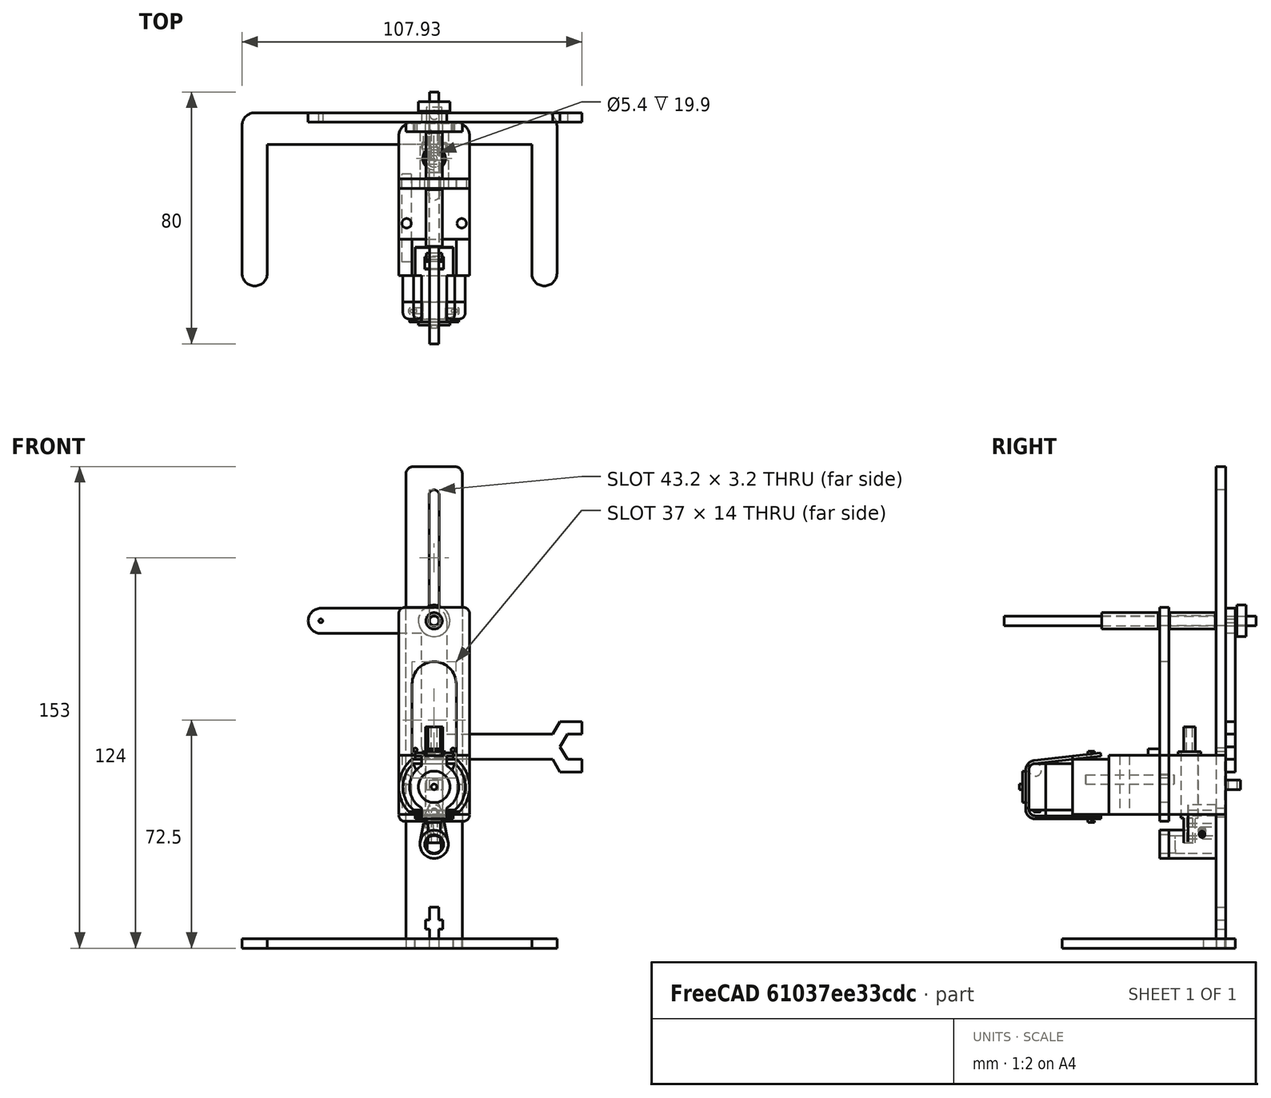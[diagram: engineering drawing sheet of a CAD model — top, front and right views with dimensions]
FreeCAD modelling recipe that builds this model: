
FCSTD DOCUMENT  (FreeCAD 0.21R33771 (Git))
Label: legged_robot_03
License: Other
LicenseURL: https://ohwr.org/project/cernohl/wikis/Documents/CERN-OHL-version-2
objects: PartDesign::Body×23, Part::Feature×19, Sketcher::SketchObject×18, PartDesign::SubShapeBinder×16, PartDesign::Pad×15, PartDesign::CoordinateSystem×12, PartDesign::FeatureBase×9, Part::Part2DObjectPython×7, PartDesign::Plane×6, App::DocumentObjectGroup×4, Part::Compound2×2, PartDesign::Pocket×2, App::FeaturePython×1, App::Part×1, App::LinkGroup×1
note: 144 computed .brp shape members not serialized (recipe doc carries the construction recipe); baked Part::Feature solids carry a one-line shape summary decoded from their .brp

FEATURE [PartDesign::CoordinateSystem] LCS_Origin
  AttacherType = Attacher::AttachEngine3D
  MapMode = 2
  Support = -> [X_Axis025]
FEATURE [App::FeaturePython] Variables  # WARN: FeaturePython — macro-defined, semantics opaque (R4)
  Type = App::PropertyContainer
FEATURE [App::DocumentObjectGroup] Constraints
FEATURE [App::DocumentObjectGroup] Configurations
FEATURE [App::Part] Assembly
  AssemblyType = Part::Link
  Group = -> [LCS_Origin,Variables,Constraints,Configurations]
  Origin = -> Origin025
  Type = Assembly
FEATURE [PartDesign::SubShapeBinder] Binder002
  BindCopyOnChange = 0
  BindMode = 0
  ClaimChildren = false
  Context = -> Parts [Body001.Binder002.]
  Fuse = false
  MakeFace = true
  OffsetFill = false
  OffsetIntersection = false
  OffsetJoinType = 0
  OffsetOpenResult = false
  PartialLoad = false
  Refine = true
  Relative = true
  Support = -> [LinkGroup]
  _Version = 2
FEATURE [PartDesign::CoordinateSystem] motor_mount_urb
  AttacherType = Attacher::AttachEngine3D
  AttachmentOffset = pos=(0,0,0) rot=(0.57735,-0.57735,-0.57735;2.0944rad)
  MapMode = 11
  Placement = pos=(-8.75,-9.5,-7.7) rot=(0,0,1;0rad)
  Support = -> [Binder002]
FEATURE [PartDesign::CoordinateSystem] motor_top_centre
  AttacherType = Attacher::AttachEngine3D
  AttachmentOffset = pos=(0,0,0) rot=(0,0,-1;1.5708rad)
  MapMode = 11
  Placement = pos=(-1.2e-15,-19.55,25.7) rot=(0,0,1;0rad)
  Support = -> [Binder002]
FEATURE [Part::Feature] Shell002
  shape: bbox 8 x 1.776 x 1.987 mm, 1 faces, 0 solids (baked)
FEATURE [Part::Feature] Solid008  label="Part 3"
  shape: bbox 19.8 x 8.5 x 14.8 mm, 6 faces (baked)
FEATURE [Part::Feature] Solid009  label="Part 2"
  shape: bbox 5.4 x 5.4 x 36.8 mm, 15 faces (baked)
FEATURE [PartDesign::CoordinateSystem] motor_mount_urf
  AttacherType = Attacher::AttachEngine3D
  AttachmentOffset = pos=(0,0,0) rot=(-0.57735,-0.57735,0.57735;2.0944rad)
  MapMode = 11
  Placement = pos=(8.75,-9.5,-7.7) rot=(0,0,1;0rad)
  Support = -> [Binder002]
FEATURE [Part::Feature] Solid003  label="Part 8"
  shape: bbox 15.62 x 23.85 x 20.96 mm, 35 faces (baked)
FEATURE [Part::Feature] Solid010  label="Part 1"
  shape: bbox 22.5 x 53.35 x 23.3 mm, 41 faces (baked)
FEATURE [PartDesign::CoordinateSystem] motor_mount_ul  label="motor_mount_ulb"
  AttacherType = Attacher::AttachEngine3D
  AttachmentOffset = pos=(0,0,0) rot=(0.57735,-0.57735,-0.57735;2.0944rad)
  MapMode = 11
  Placement = pos=(-8.75,-28.3,-7.7) rot=(0,0,1;0rad)
  Support = -> [Binder002]
FEATURE [PartDesign::CoordinateSystem] motor_cam_left
  AttacherType = Attacher::AttachEngine3D
  AttachmentOffset = pos=(0,0,0) rot=(0.57735,-0.57735,-0.57735;2.0944rad)
  MapMode = 11
  Placement = pos=(-1e-16,-37.3,-28.3) rot=(0,0,1;0rad)
  Support = -> [Binder002]
FEATURE [PartDesign::CoordinateSystem] motor_cam_right
  AttacherType = Attacher::AttachEngine3D
  AttachmentOffset = pos=(0,0,0) rot=(0.57735,-0.57735,-0.57735;2.0944rad)
  MapMode = 11
  Placement = pos=(-1e-16,-0.499998,-28.3) rot=(0,0,1;0rad)
  Support = -> [Binder002]
FEATURE [Part::Feature] Shell001
  shape: bbox 8 x 21.07 x 2.378 mm, 1 faces, 0 solids (baked)
FEATURE [PartDesign::CoordinateSystem] motor_base_centre
  AttacherType = Attacher::AttachEngine3D
  AttachmentOffset = pos=(0,0,0) rot=(-0.707107,0,-0.707107;3.14159rad)
  MapMode = 45
  Placement = pos=(-6.6e-15,-18.9,-42.1) rot=(0,1.00652,0;0rad)
  Support = -> [Binder002]
FEATURE [Part::Feature] Solid006  label="Part 5"
  shape: bbox 1.8 x 1 x 1.8 mm, 3 faces (baked)
FEATURE [Part::Feature] Solid007  label="Part 4"
  shape: bbox 21.43 x 7.35 x 17.97 mm, 16 faces (baked)
FEATURE [Part::Feature] Shell004
  shape: bbox 8 x 2 x 2 mm, 1 faces, 0 solids (baked)
FEATURE [Part::Feature] Solid004  label="Part 7"
  shape: bbox 4.343 x 2 x 0.1 mm, 16 faces (baked)
FEATURE [Part::Feature] Shell
  shape: bbox 8 x 20.85 x 2e-07 mm, 1 faces, 0 solids (baked)
FEATURE [PartDesign::CoordinateSystem] motor_mount_ulf
  AttacherType = Attacher::AttachEngine3D
  AttachmentOffset = pos=(0,0,0) rot=(-0.57735,-0.57735,0.57735;2.0944rad)
  MapMode = 11
  Placement = pos=(8.75,-28.3,-7.7) rot=(0,0,1;0rad)
  Support = -> [Binder002]
FEATURE [PartDesign::CoordinateSystem] LCS_13
  AttacherType = Attacher::AttachEngine3D
  AttachmentOffset = pos=(0,0,0) rot=(-0.57735,-0.57735,-0.57735;2.0944rad)
  MapMode = 14
  Placement = pos=(11.25,-28.3,-2.65) rot=(0,0,1;0rad)
  Support = -> [Binder002]
FEATURE [PartDesign::Body] Body001  label="Motor001"
  Group = -> [Binder002,motor_cam_left,motor_cam_right,motor_mount_ul,motor_mount_ulf,motor_mount_urb,motor_mount_urf,motor_top_centre,motor_base_centre,LCS_13]
  Origin = -> Origin001
FEATURE [Part::Feature] Solid005  label="Part 6"
  shape: bbox 4.343 x 2 x 0.1 mm, 16 faces (baked)
FEATURE [Part::Feature] Shell003
  shape: bbox 8 x 2e-07 x 12.6 mm, 1 faces, 0 solids (baked)
FEATURE [Part::Compound2] Compound001  label="Surface 1"
  Links = -> [Shell,Shell001,Shell002,Shell003,Shell004]
FEATURE [App::LinkGroup] LinkGroup
  ElementList = -> [Solid003,Compound001,Solid004,Solid005,Solid006,Solid007,Solid008,Solid009,Solid010]
  LinkMode = 0
  Placement = pos=(0,-9.5,-28.3) rot=(-1,0,0;1.5708rad)
FEATURE [Part::Feature] Shell005
  shape: bbox 25.33 x 0.8457 x 15.74 mm, 1 faces, 0 solids (baked)
FEATURE [Part::Feature] Shell006
  shape: bbox 24.78 x 2e-07 x 15.38 mm, 1 faces, 0 solids (baked)
FEATURE [Part::Feature] Shell007
  shape: bbox 26 x 42.82 x 16.6 mm, 188 faces, 0 solids (baked)
FEATURE [Part::Feature] Shell008
  shape: bbox 8.776 x 3 x 7.6 mm, 28 faces, 0 solids (baked)
FEATURE [Part::Feature] Shell009
  shape: bbox 6.35 x 1.5 x 6.35 mm, 2 faces, 0 solids (baked)
FEATURE [Part::Feature] Shell010
  shape: bbox 8 x 3.2 x 8 mm, 10 faces, 0 solids (baked)
FEATURE [Part::Compound2] Compound  label="battery_9V"
  Links = -> [Shell005,Shell006,Shell007,Shell008,Shell009,Shell010]
  Placement = pos=(-25,-19,-18) rot=(0,0.707107,0.707107;3.14159rad)
FEATURE [PartDesign::SubShapeBinder] Binder007
  BindCopyOnChange = 0
  BindMode = 0
  ClaimChildren = false
  Context = -> Parts [Body021.Binder007.]
  Fuse = false
  MakeFace = true
  OffsetFill = false
  OffsetIntersection = false
  OffsetJoinType = 0
  OffsetOpenResult = false
  PartialLoad = false
  Refine = true
  Relative = true
  Support = -> [LinkGroup]
  _Version = 2
FEATURE [Sketcher::SketchObject] Sketch027
  AttachmentOffset = pos=(0,0,2) rot=(0,0,1;0rad)
  ExternalGeometry = -> [Binder007]
  FullyConstrained = true
  MapMode = 5
  Placement = pos=(0,0,20.4) rot=(0,0,1;0rad)
  Support = -> [Binder007]
  sketch-geometry (23):
    g0: Circle CenterX=1.90735e-07 CenterY=27 CenterZ=0 NormalX=0 NormalY=0 NormalZ=1 AngleXU=0 Radius=4.5
    g1: Circle CenterX=10 CenterY=27 CenterZ=0 NormalX=0 NormalY=0 NormalZ=1 AngleXU=0 Radius=0.95
    g2: LineSegment StartX=0.900016 StartY=31.4091 StartZ=0 EndX=10.5 EndY=29.4495 EndZ=0
    g3: ArcOfCircle CenterX=10 CenterY=27 CenterZ=0 NormalX=0 NormalY=0 NormalZ=1 AngleXU=0 Radius=2.5 StartAngle=4.8601 EndAngle=7.65262
    g4: LineSegment StartX=10.3679 StartY=24.5272 StartZ=0 EndX=8.88426 EndY=24.3065 EndZ=0
    g5: ArcOfCircle CenterX=8.58992 CenterY=26.2847 CenterZ=0 NormalX=0 NormalY=0 NormalZ=1 AngleXU=0 Radius=2 StartAngle=3.2893 EndAngle=4.8601
    g6: LineSegment StartX=6.6117 StartY=25.9903 StartZ=0 EndX=6.58226 EndY=26.1882 EndZ=0
    g7: ArcOfCircle CenterX=5.84043 CenterY=26.0778 CenterZ=0 NormalX=0 NormalY=0 NormalZ=1 AngleXU=0 Radius=0.75 StartAngle=0.147708 EndAngle=1.54397
    g8: LineSegment StartX=5.86055 StartY=26.8275 StartZ=0 EndX=2.79854 EndY=26.9097 EndZ=0
    g9: LineSegment StartX=0.781434 StartY=22.5684 StartZ=0 EndX=6.69028 EndY=23.6103 EndZ=0
    g10: LineSegment StartX=6.69028 StartY=23.6103 StartZ=0 EndX=6.534 EndY=24.4966 EndZ=0
    g11: ArcOfCircle CenterX=5.54919 CenterY=24.3229 CenterZ=0 NormalX=0 NormalY=0 NormalZ=1 AngleXU=0 Radius=1 StartAngle=0.174533 EndAngle=1.5708
    g12: LineSegment StartX=5.54919 StartY=25.3229 StartZ=0 EndX=2.67887 EndY=25.3229 EndZ=0
    g13: Circle CenterX=1.90735e-07 CenterY=27 CenterZ=0 NormalX=0 NormalY=0 NormalZ=1 AngleXU=0 Radius=2.8
    g14: LineSegment StartX=1.8 StartY=29.2 StartZ=0 EndX=-1.8 EndY=29.2 EndZ=0
    g15: ArcOfCircle CenterX=-1.8 CenterY=28.2 CenterZ=0 NormalX=0 NormalY=0 NormalZ=1 AngleXU=0 Radius=1 StartAngle=1.5708 EndAngle=3.14159
    g16: LineSegment StartX=-2.8 StartY=28.2 StartZ=0 EndX=-2.8 EndY=25.8 EndZ=0
    g17: ArcOfCircle CenterX=-1.8 CenterY=25.8 CenterZ=0 NormalX=0 NormalY=0 NormalZ=1 AngleXU=0 Radius=1 StartAngle=3.14159 EndAngle=4.71239
    g18: LineSegment StartX=-1.8 StartY=24.8 StartZ=0 EndX=1.8 EndY=24.8 EndZ=0
    g19: ArcOfCircle CenterX=1.8 CenterY=25.8 CenterZ=0 NormalX=0 NormalY=0 NormalZ=1 AngleXU=0 Radius=1 StartAngle=4.71239 EndAngle=6.28319
    g20: LineSegment StartX=2.8 StartY=25.8 StartZ=0 EndX=2.8 EndY=28.2 EndZ=0
    g21: ArcOfCircle CenterX=1.8 CenterY=28.2 CenterZ=0 NormalX=0 NormalY=0 NormalZ=1 AngleXU=0 Radius=1 StartAngle=-1.8e-15 EndAngle=1.5708
    g22: LineSegment StartX=1.90735e-07 StartY=27 StartZ=0 EndX=-2.8 EndY=27 EndZ=0
  constraints (58):
    c: Diameter(g0) = 9
    c: Diameter(g1) = 1.9
    c: Tangent(g2,g3) = 1.5708
    c: Tangent(g4,g5) = 1.5708
    c: Tangent(g6,g7) = -1.5708
    c: Coincident(g9,g10)
    c: Tangent(g10,g11) = -1.5708
    c: Diameter(g3) = 5
    c: Tangent(g2,g0)
    c: PointOnObject(g2,g0)
    c: Tangent(g3,g4) = 1.5708
    c: Angle(g3) = 2.79253
    c: Distance(g4) = 1.5
    c: Diameter(g5) = 4
    c: Angle(g5) = 1.5708
    c: Tangent(g7,g8) = -1.5708
    c: Tangent(g5,g6) = 1.5708
    c: Distance(g6) = 0.2
    c: Diameter(g7) = 1.5
    c: Angle(g7) = 1.39626
    c: PointOnObject(g9,g0)
    c: Diameter(g11) = 2
    c: Distance(g10) = 0.9
    c: Perpendicular(g9,g10)
    c: Tangent(g11,g12) = -1.5708
    c: Angle(g9) = 0.174533
    c: Angle(g11) = 1.39626
    c: Tangent(g9,g0)
    c: Distance(g9) = 6
    c: Coincident(g0,g-3)
    c: Horizontal(g3,g0)
    c: DistanceX(g0,g3) = 10
    c: Coincident(g1,g3)
    c: Coincident(g13,g0)
    c: Diameter(g13) = 5.6
    c: Horizontal(g14)
    c: Tangent(g14,g15) = -1.5708
    c: Vertical(g16)
    c: Tangent(g16,g17) = -1.5708
    c: Horizontal(g18)
    c: Tangent(g18,g19) = -1.5708
    c: Vertical(g20)
    c: Tangent(g20,g21) = -1.5708
    c: Tangent(g21,g14) = -1.5708
    c: Tangent(g19,g20) = -1.5708
    c: Tangent(g17,g18) = -1.5708
    c: Tangent(g15,g16) = -1.5708
    c: Diameter(g19) = 2
    c: Equal(g19,g21)
    c: Equal(g19,g17)
    c: DistanceX(g15,g20) = 5.6
    c: DistanceY(g17,g14) = 4.4
    c: Symmetric(g15,g20,g-2)
    c: Coincident(g22,g0)
    c: PointOnObject(g22,g16)
    c: Symmetric(g14,g17,g22)
    c: PointOnObject(g8,g13)
    c: PointOnObject(g12,g19)
FEATURE [Sketcher::SketchObject] Sketch
  AttachmentOffset = pos=(0,0,2) rot=(0,0,1;0rad)
  ExternalGeometry = -> [Binder007,Sketch027]
  FullyConstrained = true
  MapMode = 5
  Placement = pos=(0,0,12.5) rot=(0,0,1;0rad)
  Support = -> [Binder007]
  sketch-geometry (2):
    g0: Circle CenterX=1.90735e-07 CenterY=27 CenterZ=0 NormalX=0 NormalY=0 NormalZ=1 AngleXU=0 Radius=2.8
    g1: Circle CenterX=1.90735e-07 CenterY=27 CenterZ=0 NormalX=0 NormalY=0 NormalZ=1 AngleXU=0 Radius=4.5
  constraints (4):
    c: Coincident(g0,g-3)
    c: Coincident(g1,g0)
    c: Equal(g0,g-5)
    c: Equal(g-4,g1)
FEATURE [PartDesign::Pad] Pad
  Direction = (1,1,1)
  Length = 2
  Length2 = 100
  Profile = -> Sketch
  Type = 0
FEATURE [Sketcher::SketchObject] Sketch029
  ExternalGeometry = -> [Binder007,Sketch027]
  FullyConstrained = true
  MapMode = 5
  Placement = pos=(3e-15,0,14.5) rot=(0,0,1;0rad)
  Support = -> [Pad]
  sketch-geometry (9):
    g0: Circle CenterX=1.90735e-07 CenterY=27 CenterZ=0 NormalX=0 NormalY=0 NormalZ=1 AngleXU=0 Radius=4.5
    g1: LineSegment StartX=1.8 StartY=29.2 StartZ=0 EndX=-1.8 EndY=29.2 EndZ=0
    g2: ArcOfCircle CenterX=-1.8 CenterY=28.2 CenterZ=0 NormalX=0 NormalY=0 NormalZ=1 AngleXU=0 Radius=1 StartAngle=1.5708 EndAngle=3.14159
    g3: LineSegment StartX=-2.8 StartY=28.2 StartZ=0 EndX=-2.8 EndY=25.8 EndZ=0
    g4: ArcOfCircle CenterX=-1.8 CenterY=25.8 CenterZ=0 NormalX=0 NormalY=0 NormalZ=1 AngleXU=0 Radius=1 StartAngle=3.14159 EndAngle=4.71239
    g5: LineSegment StartX=-1.8 StartY=24.8 StartZ=0 EndX=1.8 EndY=24.8 EndZ=0
    g6: ArcOfCircle CenterX=1.8 CenterY=25.8 CenterZ=0 NormalX=0 NormalY=0 NormalZ=1 AngleXU=0 Radius=1 StartAngle=4.71239 EndAngle=6.28319
    g7: LineSegment StartX=2.8 StartY=25.8 StartZ=0 EndX=2.8 EndY=28.2 EndZ=0
    g8: ArcOfCircle CenterX=1.8 CenterY=28.2 CenterZ=0 NormalX=0 NormalY=0 NormalZ=1 AngleXU=0 Radius=1 StartAngle=-1.8e-15 EndAngle=1.5708
  constraints (17):
    c: Coincident(g0,g-4)
    c: Coincident(g-5,g1)
    c: Coincident(g1,g-5)
    c: Tangent(g1,g2) = -1.5708
    c: Coincident(g3,g-7)
    c: Tangent(g3,g4) = -1.5708
    c: Coincident(g5,g-6)
    c: Tangent(g5,g6) = -1.5708
    c: Coincident(g7,g-8)
    c: Tangent(g7,g8) = -1.5708
    c: Tangent(g2,g3) = -1.5708
    c: Tangent(g4,g5) = -1.5708
    c: Tangent(g6,g7) = -1.5708
    c: Tangent(g8,g1) = -1.5708
    c: Vertical(g3)
    c: Horizontal(g5)
    c: Equal(g0,g-4)
FEATURE [PartDesign::Pad] Pad029
  BaseFeature = -> Pad
  Direction = (1,1,1)
  Length = 4
  Length2 = 100
  Profile = -> Sketch029
  Type = 0
FEATURE [Sketcher::SketchObject] Sketch028
  ExternalGeometry = -> [Sketch027]
  FullyConstrained = true
  MapMode = 5
  Placement = pos=(3.5e-15,0,18.5) rot=(0,0,1;0rad)
  Support = -> [Pad029]
  sketch-geometry (21):
    g0: LineSegment StartX=10.5 StartY=29.4495 StartZ=0 EndX=0.900016 EndY=31.4091 EndZ=0
    g1: ArcOfCircle CenterX=1.69849e-05 CenterY=27 CenterZ=0 NormalX=0 NormalY=0 NormalZ=1 AngleXU=0 Radius=4.5 StartAngle=1.36944 EndAngle=4.88692
    g2: LineSegment StartX=0.781434 StartY=22.5684 StartZ=0 EndX=6.69028 EndY=23.6103 EndZ=0
    g3: LineSegment StartX=6.69028 StartY=23.6103 StartZ=0 EndX=6.534 EndY=24.4966 EndZ=0
    g4: ArcOfCircle CenterX=5.54919 CenterY=24.3229 CenterZ=0 NormalX=0 NormalY=0 NormalZ=1 AngleXU=0 Radius=1 StartAngle=0.174533 EndAngle=1.5708
    g5: LineSegment StartX=5.54919 StartY=25.3229 StartZ=0 EndX=2.8 EndY=25.8 EndZ=0
    g6: ArcOfCircle CenterX=1.59004 CenterY=26.01 CenterZ=0 NormalX=0 NormalY=0 NormalZ=1 AngleXU=0 Radius=1.22805 StartAngle=4.88421 EndAngle=6.11137
    g7: LineSegment StartX=1.8 StartY=24.8 StartZ=0 EndX=-1.8 EndY=24.8 EndZ=0
    g8: ArcOfCircle CenterX=-1.8 CenterY=25.8 CenterZ=0 NormalX=0 NormalY=0 NormalZ=1 AngleXU=0 Radius=1 StartAngle=3.14159 EndAngle=4.71239
    g9: LineSegment StartX=-2.8 StartY=25.8 StartZ=0 EndX=-2.8 EndY=28.2 EndZ=0
    g10: ArcOfCircle CenterX=-1.8 CenterY=28.2 CenterZ=0 NormalX=0 NormalY=0 NormalZ=1 AngleXU=0 Radius=1 StartAngle=1.5708 EndAngle=3.14159
    g11: LineSegment StartX=-1.8 StartY=29.2 StartZ=0 EndX=1.8 EndY=29.2 EndZ=0
    g12: ArcOfCircle CenterX=1.8 CenterY=28.2 CenterZ=0 NormalX=0 NormalY=0 NormalZ=1 AngleXU=0 Radius=1 StartAngle=5e-16 EndAngle=1.5708
    g13: LineSegment StartX=2.8 StartY=28.2 StartZ=0 EndX=2.79854 EndY=26.9097 EndZ=0
    g14: LineSegment StartX=2.79854 StartY=26.9097 StartZ=0 EndX=5.86055 EndY=26.8275 EndZ=0
    g15: ArcOfCircle CenterX=5.84043 CenterY=26.0778 CenterZ=0 NormalX=0 NormalY=0 NormalZ=1 AngleXU=0 Radius=0.75 StartAngle=0.147708 EndAngle=1.54397
    g16: LineSegment StartX=6.58226 StartY=26.1882 StartZ=0 EndX=6.6117 EndY=25.9903 EndZ=0
    g17: ArcOfCircle CenterX=8.58992 CenterY=26.2847 CenterZ=0 NormalX=0 NormalY=0 NormalZ=1 AngleXU=0 Radius=2 StartAngle=3.2893 EndAngle=4.8601
    g18: LineSegment StartX=8.88426 StartY=24.3065 StartZ=0 EndX=10.3679 EndY=24.5272 EndZ=0
    g19: ArcOfCircle CenterX=10 CenterY=27 CenterZ=0 NormalX=0 NormalY=0 NormalZ=1 AngleXU=0 Radius=2.5 StartAngle=4.8601 EndAngle=7.65262
    g20: Circle CenterX=10 CenterY=27 CenterZ=0 NormalX=0 NormalY=0 NormalZ=1 AngleXU=0 Radius=0.95
  constraints (42):
    c: Coincident(g-6,g0)
    c: Coincident(g0,g-6)
    c: Tangent(g0,g1) = -1.5708
    c: Coincident(g1,g-17)
    c: Coincident(g1,g2)
    c: Coincident(g2,g-17)
    c: Coincident(g2,g3)
    c: Coincident(g3,g-15)
    c: Tangent(g3,g4) = -1.5708
    c: Coincident(g4,g-8)
    c: Coincident(g4,g5)
    c: Coincident(g5,g-16)
    c: Perpendicular(g5,g6) = 4.71239
    c: Coincident(g6,g-16)
    c: Coincident(g6,g7)
    c: Coincident(g7,g-14)
    c: Tangent(g7,g8) = 1.5708
    c: Coincident(g8,g-14)
    c: Coincident(g8,g9)
    c: Coincident(g9,g-11)
    c: Tangent(g9,g10) = 1.5708
    c: Coincident(g10,g-21)
    c: Coincident(g10,g11)
    c: Coincident(g11,g-22)
    c: Tangent(g11,g12) = 1.5708
    c: Coincident(g12,g-22)
    c: Coincident(g12,g13)
    c: Coincident(g13,g-3)
    c: Coincident(g13,g14)
    c: Coincident(g14,g-19)
    c: Tangent(g14,g15) = 1.5708
    c: Coincident(g15,g-19)
    c: Coincident(g15,g16)
    c: Coincident(g16,g-18)
    c: Tangent(g16,g17) = -1.5708
    c: Coincident(g17,g-18)
    c: Coincident(g17,g18)
    c: Coincident(g18,g-7)
    c: Tangent(g18,g19) = -1.5708
    c: Coincident(g19,g0)
    c: Coincident(g20,g19)
    c: Equal(g-20,g20)
FEATURE [PartDesign::Pad] Pad030
  BaseFeature = -> Pad029
  Direction = (1,1,1)
  Length = 9
  Length2 = 100
  Profile = -> Sketch028
  Type = 0
FEATURE [Sketcher::SketchObject] Sketch031
  ExternalGeometry = -> [Pad030]
  FullyConstrained = true
  MapMode = 5
  Placement = pos=(-3.83586,21.7542,7e-16) rot=(0.992433,0.086827,0.086827;1.57839rad)
  Support = -> [Pad030]
  sketch-geometry (2):
    g0: Circle CenterX=8.48852 CenterY=23 CenterZ=0 NormalX=0 NormalY=0 NormalZ=1 AngleXU=0 Radius=0.95
    g1: LineSegment StartX=8.48852 StartY=23 StartZ=0 EndX=10.6885 EndY=23 EndZ=0
  constraints (5):
    c: Diameter(g0) = 1.9
    c: Coincident(g1,g0)
    c: Horizontal(g1)
    c: DistanceX(g1,g1) = 2.2
    c: Symmetric(g-3,g-3,g1)
FEATURE [PartDesign::Pocket] Pocket
  BaseFeature = -> Pad030
  Direction = (1,1,1)
  Length = 5
  Length2 = 100
  Profile = -> Sketch031
  Type = 1
FEATURE [Sketcher::SketchObject] Sketch030
  ExternalGeometry = -> [Pocket]
  FullyConstrained = true
  MapMode = 5
  Placement = pos=(-3.83586,21.7542,7e-16) rot=(0.992433,0.086827,0.086827;1.57839rad)
  Support = -> [Pocket]
  sketch-geometry (1):
    g0: Circle CenterX=8.48852 CenterY=23 CenterZ=0 NormalX=0 NormalY=0 NormalZ=1 AngleXU=0 Radius=1.1
  constraints (2):
    c: Diameter(g0) = 2.2
    c: Coincident(g0,g-3)
FEATURE [PartDesign::Pocket] Pocket001
  BaseFeature = -> Pocket
  Direction = (1,1,1)
  Length = 0
  Length2 = 100
  Profile = -> Sketch030
  Type = 3
  UpToFace = -> Pocket [Face19]
FEATURE [PartDesign::CoordinateSystem] LCS_1
  AttacherType = Attacher::AttachEngine3D
  AttachmentOffset = pos=(0,0,0) rot=(-1,0,0;1.5708rad)
  MapMode = 11
  Placement = pos=(10,27,27.5) rot=(-0.57735,-0.57735,0.57735;2.0944rad)
  Support = -> [Pocket001]
FEATURE [PartDesign::CoordinateSystem] LCS_2
  AttacherType = Attacher::AttachEngine3D
  AttachmentOffset = pos=(0,0,0) rot=(-1,0,0;1.5708rad)
  MapMode = 11
  Placement = pos=(1.90735e-07,27,12.5) rot=(-0.57735,-0.57735,0.57735;2.0944rad)
  Support = -> [Pocket001]
FEATURE [PartDesign::Body] Body021  label="cam_3Dp_motor_left"
  Group = -> [Sketch027,Sketch028,Sketch029,Sketch030,Sketch031,Sketch,Binder007,Pad,Pad029,Pad030,Pocket,Pocket001,LCS_1,LCS_2]
  Origin = -> Origin024
  Placement = pos=(-27,-18.9,-28.3) rot=(0.57735,0.57735,-0.57735;2.0944rad)
  Tip = -> Pocket001
FEATURE [PartDesign::SubShapeBinder] Binder
  BindCopyOnChange = 0
  BindMode = 0
  ClaimChildren = false
  Context = -> Parts [Body.Binder.]
  Fuse = false
  MakeFace = true
  OffsetFill = false
  OffsetIntersection = false
  OffsetJoinType = 0
  OffsetOpenResult = false
  PartialLoad = false
  Refine = true
  Relative = true
  Support = -> [Body021]
  _Version = 2
FEATURE [Sketcher::SketchObject] Sketch032
  ExternalGeometry = -> [Binder]
  FullyConstrained = true
  MapMode = 5
  Placement = pos=(4.6e-15,-46.4,-8.8e-15) rot=(0,0.707107,0.707107;3.14159rad)
  Support = -> [Binder]
  sketch-geometry (35):
    g0: LineSegment StartX=-6.5 StartY=71.7 StartZ=0 EndX=6.5 EndY=71.7 EndZ=0
    g1: LineSegment StartX=9 StartY=69.2 StartZ=0 EndX=9 EndY=-78.3 EndZ=0
    g2: LineSegment StartX=6 StartY=-78.3 StartZ=0 EndX=1.5 EndY=-78.3 EndZ=0
    g3: LineSegment StartX=-9 StartY=-78.3 StartZ=0 EndX=-9 EndY=69.2 EndZ=0
    g4: Circle CenterX=-7.1e-15 CenterY=-38.3 CenterZ=0 NormalX=0 NormalY=0 NormalZ=1 AngleXU=0 Radius=1.4
    g5: ArcOfCircle CenterX=-3.3e-15 CenterY=62.7 CenterZ=0 NormalX=0 NormalY=0 NormalZ=1 AngleXU=0 Radius=1.6 StartAngle=-9e-16 EndAngle=3.14159
    g6: ArcOfCircle CenterX=-3.3e-15 CenterY=22.7 CenterZ=0 NormalX=0 NormalY=0 NormalZ=1 AngleXU=0 Radius=1.6 StartAngle=3.14159 EndAngle=6.28319
    g7: LineSegment StartX=-1.6 StartY=62.7 StartZ=0 EndX=-1.6 EndY=22.7 EndZ=0
    g8: LineSegment StartX=1.6 StartY=62.7 StartZ=0 EndX=1.6 EndY=22.7 EndZ=0
    g9: LineSegment StartX=-7.1e-15 StartY=-38.3 StartZ=0 EndX=-3.3e-15 EndY=22.7 EndZ=0
    g10: LineSegment StartX=-3.3e-15 StartY=62.7 StartZ=0 EndX=-3.3e-15 EndY=71.7 EndZ=0
    g11: LineSegment StartX=-3.3e-15 StartY=22.7 StartZ=0 EndX=-3.3e-15 EndY=42.7 EndZ=0
    g12: LineSegment StartX=-3.3e-15 StartY=42.7 StartZ=0 EndX=-3.3e-15 EndY=62.7 EndZ=0
    g13: Circle CenterX=6 CenterY=-18.3 CenterZ=0 NormalX=0 NormalY=0 NormalZ=1 AngleXU=0 Radius=0.6
    g14: Circle CenterX=-6 CenterY=-18.3 CenterZ=0 NormalX=0 NormalY=0 NormalZ=1 AngleXU=0 Radius=0.6
    g15: ArcOfCircle CenterX=-6.5 CenterY=69.2 CenterZ=0 NormalX=0 NormalY=0 NormalZ=1 AngleXU=0 Radius=2.5 StartAngle=1.5708 EndAngle=3.14159
    g16: ArcOfCircle CenterX=6.5 CenterY=69.2 CenterZ=0 NormalX=0 NormalY=0 NormalZ=1 AngleXU=0 Radius=2.5 StartAngle=8e-16 EndAngle=1.5708
    g17: LineSegment StartX=-1.5 StartY=-78.3 StartZ=0 EndX=-1.5 EndY=-75.3 EndZ=0
    g18: LineSegment StartX=-1.5 StartY=-75.3 StartZ=0 EndX=-2.75 EndY=-75.3 EndZ=0
    g19: LineSegment StartX=-2.75 StartY=-75.3 StartZ=0 EndX=-2.75 EndY=-72.3 EndZ=0
    g20: LineSegment StartX=-2.75 StartY=-72.3 StartZ=0 EndX=-1.5 EndY=-72.3 EndZ=0
    g21: LineSegment StartX=-1.5 StartY=-72.3 StartZ=0 EndX=-1.5 EndY=-68.3 EndZ=0
    g22: LineSegment StartX=-1.5 StartY=-68.3 StartZ=0 EndX=1.5 EndY=-68.3 EndZ=0
    g23: LineSegment StartX=1.5 StartY=-68.3 StartZ=0 EndX=1.5 EndY=-72.3 EndZ=0
    g24: LineSegment StartX=1.5 StartY=-72.3 StartZ=0 EndX=2.75 EndY=-72.3 EndZ=0
    g25: LineSegment StartX=2.75 StartY=-72.3 StartZ=0 EndX=2.75 EndY=-75.3 EndZ=0
    g26: LineSegment StartX=2.75 StartY=-75.3 StartZ=0 EndX=1.5 EndY=-75.3 EndZ=0
    g27: LineSegment StartX=1.5 StartY=-75.3 StartZ=0 EndX=1.5 EndY=-78.3 EndZ=0
    g28: LineSegment StartX=-1.5 StartY=-78.3 StartZ=0 EndX=-6 EndY=-78.3 EndZ=0
    g29: LineSegment StartX=-9 StartY=-78.3 StartZ=0 EndX=-9 EndY=-81.3 EndZ=0
    g30: LineSegment StartX=-9 StartY=-81.3 StartZ=0 EndX=-6 EndY=-81.3 EndZ=0
    g31: LineSegment StartX=-6 StartY=-81.3 StartZ=0 EndX=-6 EndY=-78.3 EndZ=0
    g32: LineSegment StartX=9 StartY=-78.3 StartZ=0 EndX=9 EndY=-81.3 EndZ=0
    g33: LineSegment StartX=9 StartY=-81.3 StartZ=0 EndX=6 EndY=-81.3 EndZ=0
    g34: LineSegment StartX=6 StartY=-81.3 StartZ=0 EndX=6 EndY=-78.3 EndZ=0
  constraints (98):
    c: Tangent(g5,g8) = 1.5708
    c: Tangent(g5,g7) = -1.5708
    c: Tangent(g7,g6) = -1.5708
    c: Tangent(g8,g6) = 1.5708
    c: Equal(g5,g6)
    c: Diameter(g4) = 2.8
    c: Coincident(g9,g4)
    c: Coincident(g9,g6)
    c: Coincident(g10,g5)
    c: Diameter(g6) = 3.2
    c: Distance(g10) = 9
    c: Angle(g3,g0) = 1.5708
    c: Angle(g0,g1) = 1.5708
    c: Angle(g2,g3) = 1.5708
    c: Parallel(g3,g10)
    c: Coincident(g11,g6)
    c: Coincident(g12,g11)
    c: Coincident(g12,g5)
    c: Parallel(g11,g12)
    c: Parallel(g12,g10)
    c: Equal(g12,g11)
    c: Distance(g12) = 20
    c: Coincident(g4,g-3)
    c: Angle(g9) = 1.5708
    c: DistanceY(g4,g13) = 20
    c: Distance(g13,g1) = 3
    c: Horizontal(g14,g13)
    c: Distance(g14,g3) = 3
    c: Tangent(g0,g15) = 1.5708
    c: Tangent(g3,g15) = 1.5708
    c: Tangent(g0,g16) = 1.5708
    c: Tangent(g1,g16) = 1.5708
    c: Distance(g0,g2) = 150
    c: Diameter(g16) = 5
    c: Equal(g16,g15)
    c: Symmetric(g0,g0,g10)
    c: DistanceX(g3,g1) = 18
    c: PointOnObject(g17,g2)
    c: Vertical(g17)
    c: Coincident(g17,g18)
    c: Horizontal(g18)
    c: Coincident(g18,g19)
    c: Vertical(g19)
    c: Coincident(g19,g20)
    c: Horizontal(g20)
    c: Coincident(g20,g21)
    c: Vertical(g21)
    c: Coincident(g21,g22)
    c: Coincident(g22,g23)
    c: Vertical(g23)
    c: Coincident(g23,g24)
    c: Horizontal(g24)
    c: Coincident(g24,g25)
    c: Vertical(g25)
    c: Coincident(g25,g26)
    c: Horizontal(g26)
    c: Coincident(g26,g27)
    c: Vertical(g27)
    c: Equal(g21,g23)
    c: Equal(g20,g18)
    c: Equal(g18,g24)
    c: Equal(g24,g26)
    c: Equal(g19,g25)
    c: DistanceX(g22,g22) = 3
    c: DistanceX(g19,g24) = 5.5
    c: DistanceY(g19,g19) = 3
    c: DistanceY(g17,g17) = 3
    c: DistanceY(g21,g21) = 4
    c: Coincident(g2,g27)
    c: Tangent(g2,g28)
    c: PointOnObject(g28,g17)
    c: Coincident(g3,g29)
    c: Vertical(g29)
    c: Coincident(g29,g30)
    c: Horizontal(g30)
    c: Coincident(g30,g31)
    c: Vertical(g31)
    c: Coincident(g1,g32)
    c: Vertical(g32)
    c: Coincident(g32,g33)
    c: Horizontal(g33)
    c: Coincident(g33,g34)
    c: Vertical(g34)
    c: Equal(g31,g34)
    c: Equal(g30,g33)
    c: DistanceX(g30,g30) = 3
    c: DistanceY(g29,g29) = 3
    c: Coincident(g28,g31)
    c: Coincident(g2,g34)
    c: Equal(g2,g28)
    c: Equal(g3,g1)
    c: Horizontal(g28,g3)
    c: Vertical(g3)
    c: Diameter(g13) = 1.2
    c: Equal(g13,g14)
    c: DistanceY(g9,g9) = 61
    c: Horizontal(g22)
    c: DistanceY(g33,g4) = 43
FEATURE [PartDesign::Pad] Pad026
  Direction = (-1e-16,1,2e-16)
  Length = 3
  Length2 = 100
  Profile = -> Sketch032
  Reversed = true
  Type = 0
FEATURE [PartDesign::SubShapeBinder] Binder008
  BindCopyOnChange = 0
  BindMode = 0
  ClaimChildren = false
  Context = -> Parts [Body.Binder008.]
  Fuse = false
  MakeFace = true
  OffsetFill = false
  OffsetIntersection = false
  OffsetJoinType = 0
  OffsetOpenResult = false
  PartialLoad = false
  Refine = true
  Relative = true
  Support = -> [LinkGroup]
  _Version = 2
FEATURE [PartDesign::Body] Body  label="leg_left"
  Group = -> [Sketch032,Pad026,Binder,Binder008]
  Origin = -> Origin
  Tip = -> Pad026
FEATURE [PartDesign::SubShapeBinder] Binder009
  BindCopyOnChange = 0
  BindMode = 0
  ClaimChildren = false
  Context = -> Body022 [Binder009.]
  Fuse = false
  MakeFace = true
  OffsetFill = false
  OffsetIntersection = false
  OffsetJoinType = 0
  OffsetOpenResult = false
  PartialLoad = false
  Refine = true
  Relative = true
  Support = -> [Body]
  _Version = 2
FEATURE [Sketcher::SketchObject] Sketch033
  ExternalGeometry = -> [Binder009]
  FullyConstrained = true
  MapMode = 5
  Placement = pos=(0,1.67e-14,-75.3) rot=(0,1,0;3.14159rad)
  Support = -> [Binder009]
  sketch-geometry (22):
    g0: LineSegment StartX=53 StartY=1.4 StartZ=0 EndX=53 EndY=42.4 EndZ=0
    g1: LineSegment StartX=-31 StartY=42.4 StartZ=0 EndX=-31 EndY=1.4 EndZ=0
    g2: LineSegment StartX=-39 StartY=1.4 StartZ=0 EndX=-39 EndY=48.4 EndZ=0
    g3: LineSegment StartX=-35 StartY=52.4 StartZ=0 EndX=-9 EndY=52.4 EndZ=0
    g4: LineSegment StartX=9 StartY=52.4 StartZ=0 EndX=57 EndY=52.4 EndZ=0
    g5: LineSegment StartX=61 StartY=48.4 StartZ=0 EndX=61 EndY=1.4 EndZ=0
    g6: ArcOfCircle CenterX=57 CenterY=48.4 CenterZ=0 NormalX=0 NormalY=0 NormalZ=1 AngleXU=0 Radius=4 StartAngle=-9e-16 EndAngle=1.5708
    g7: ArcOfCircle CenterX=-35 CenterY=48.4 CenterZ=0 NormalX=0 NormalY=0 NormalZ=1 AngleXU=0 Radius=4 StartAngle=1.5708 EndAngle=3.14159
    g8: ArcOfCircle CenterX=57 CenterY=1.4 CenterZ=0 NormalX=0 NormalY=0 NormalZ=1 AngleXU=0 Radius=4 StartAngle=3.14159 EndAngle=6.28319
    g9: ArcOfCircle CenterX=-35 CenterY=1.4 CenterZ=0 NormalX=0 NormalY=0 NormalZ=1 AngleXU=0 Radius=4 StartAngle=3.14159 EndAngle=6.28319
    g10: LineSegment StartX=-31 StartY=42.4 StartZ=0 EndX=53 EndY=42.4 EndZ=0
    g11: LineSegment StartX=-9 StartY=52.4 StartZ=0 EndX=9 EndY=52.4 EndZ=0
    g12: LineSegment StartX=-6 StartY=47.9 StartZ=0 EndX=0 EndY=47.9 EndZ=0
    g13: Circle CenterX=0 CenterY=47.9 CenterZ=0 NormalX=0 NormalY=0 NormalZ=1 AngleXU=0 Radius=1.5
    g14: LineSegment StartX=-8.8 StartY=49.2 StartZ=0 EndX=-6.2 EndY=49.2 EndZ=0
    g15: LineSegment StartX=-6.2 StartY=49.2 StartZ=0 EndX=-6.2 EndY=46.6 EndZ=0
    g16: LineSegment StartX=-6.2 StartY=46.6 StartZ=0 EndX=-8.8 EndY=46.6 EndZ=0
    g17: LineSegment StartX=-8.8 StartY=46.6 StartZ=0 EndX=-8.8 EndY=49.2 EndZ=0
    g18: LineSegment StartX=6.2 StartY=49.2 StartZ=0 EndX=8.8 EndY=49.2 EndZ=0
    g19: LineSegment StartX=8.8 StartY=49.2 StartZ=0 EndX=8.8 EndY=46.6 EndZ=0
    g20: LineSegment StartX=8.8 StartY=46.6 StartZ=0 EndX=6.2 EndY=46.6 EndZ=0
    g21: LineSegment StartX=6.2 StartY=46.6 StartZ=0 EndX=6.2 EndY=49.2 EndZ=0
  constraints (61):
    c: Tangent(g5,g6) = 1.5708
    c: Tangent(g4,g6) = 1.5708
    c: Tangent(g2,g7) = 1.5708
    c: Tangent(g3,g7) = 1.5708
    c: Diameter(g7) = 8
    c: Equal(g7,g6)
    c: Diameter(g8) = 8
    c: Equal(g9,g8)
    c: Tangent(g1,g9) = 1.5708
    c: Coincident(g10,g1)
    c: Coincident(g10,g0)
    c: Angle(g10,g0) = 1.5708
    c: Parallel(g4,g10)
    c: Parallel(g0,g5)
    c: Tangent(g8,g0) = 1.5708
    c: Angle(g1,g10) = 1.5708
    c: Parallel(g1,g2)
    c: Parallel(g10,g3)
    c: Distance(g7,g9) = 47
    c: Distance(g6,g8) = 47
    c: Distance(g6,g7) = 92
    c: Distance(g4) = 48
    c: Distance(g1) = 41
    c: Tangent(g2,g9) = 1.5708
    c: Tangent(g5,g8) = 1.5708
    c: Horizontal(g10)
    c: Coincident(g11,g3)
    c: Coincident(g11,g4)
    c: Horizontal(g11)
    c: Vertical(g4,g-3)
    c: DistanceX(g3,g3) = 26
    c: DistanceY(g-4,g3) = 3
    c: PointOnObject(g12,g-5)
    c: Symmetric(g-5,g-5,g12)
    c: PointOnObject(g12,g-2)
    c: Coincident(g13,g12)
    c: Diameter(g13) = 3
    c: Coincident(g14,g15)
    c: Coincident(g15,g16)
    c: Coincident(g16,g17)
    c: Coincident(g17,g14)
    c: Horizontal(g14)
    c: Horizontal(g16)
    c: Vertical(g15)
    c: Vertical(g17)
    c: Coincident(g18,g19)
    c: Coincident(g19,g20)
    c: Coincident(g20,g21)
    c: Coincident(g21,g18)
    c: Horizontal(g18)
    c: Horizontal(g20)
    c: Vertical(g19)
    c: Vertical(g21)
    c: Equal(g18,g14)
    c: Equal(g17,g19)
    c: DistanceX(g-4,g14) = 0.2
    c: DistanceY(g14,g-4) = 0.2
    c: DistanceX(g15,g-5) = 0.2
    c: DistanceY(g-5,g15) = 0.2
    c: Symmetric(g18,g14,g-2)
    c: DistanceX(g13,g5) = 61
FEATURE [PartDesign::Pad] Pad031
  Direction = (1,1,1)
  Length = 3
  Length2 = 100
  Profile = -> Sketch033
  Reversed = true
  Type = 0
FEATURE [PartDesign::Body] Body022  label="feet_left"
  Group = -> [Sketch033,Binder009,Pad031]
  Origin = -> Origin026
  Tip = -> Pad031
FEATURE [PartDesign::SubShapeBinder] Binder012
  BindCopyOnChange = 0
  BindMode = 0
  ClaimChildren = false
  Context = -> Parts [Body024.Binder012.]
  Fuse = false
  MakeFace = true
  OffsetFill = false
  OffsetIntersection = false
  OffsetJoinType = 0
  OffsetOpenResult = false
  PartialLoad = false
  Refine = true
  Relative = true
  Support = -> [Body]
  _Version = 2
FEATURE [PartDesign::SubShapeBinder] Binder013
  BindCopyOnChange = 0
  BindMode = 0
  ClaimChildren = false
  Context = -> Parts [Body024.Binder013.]
  Fuse = false
  MakeFace = true
  OffsetFill = false
  OffsetIntersection = false
  OffsetJoinType = 0
  OffsetOpenResult = false
  PartialLoad = false
  Refine = true
  Relative = true
  Support = -> [LinkGroup]
  _Version = 2
FEATURE [PartDesign::SubShapeBinder] Binder014
  BindCopyOnChange = 0
  BindMode = 0
  ClaimChildren = false
  Context = -> Parts [Body024.Binder014.]
  Fuse = false
  MakeFace = true
  OffsetFill = false
  OffsetIntersection = false
  OffsetJoinType = 0
  OffsetOpenResult = false
  PartialLoad = false
  Refine = true
  Relative = true
  Support = -> [Body021]
  _Version = 2
FEATURE [Sketcher::SketchObject] Sketch035
  ExternalGeometry = -> [Binder013,Binder014,Binder012]
  FullyConstrained = true
  MapMode = 5
  Placement = pos=(0,-28.3,0) rot=(1,0,0;1.5708rad)
  Support = -> [Binder013]
  sketch-geometry (18):
    g0: LineSegment StartX=0 StartY=42.7 StartZ=0 EndX=-1.09e-14 EndY=62.7 EndZ=0
    g1: LineSegment StartX=9.25 StartY=-21 StartZ=0 EndX=-9.25 EndY=-21 EndZ=0
    g2: ArcOfCircle CenterX=-9.25 CenterY=-19 CenterZ=0 NormalX=0 NormalY=0 NormalZ=1 AngleXU=0 Radius=2 StartAngle=3.14159 EndAngle=4.71239
    g3: LineSegment StartX=-11.25 StartY=-19 StartZ=0 EndX=-11.25 EndY=45 EndZ=0
    g4: ArcOfCircle CenterX=-9.25 CenterY=45 CenterZ=0 NormalX=0 NormalY=0 NormalZ=1 AngleXU=0 Radius=2 StartAngle=1.5708 EndAngle=3.14159
    g5: LineSegment StartX=-9.25 StartY=47 StartZ=0 EndX=9.25 EndY=47 EndZ=0
    g6: ArcOfCircle CenterX=9.25 CenterY=45 CenterZ=0 NormalX=0 NormalY=0 NormalZ=1 AngleXU=0 Radius=2 StartAngle=4e-16 EndAngle=1.5708
    g7: LineSegment StartX=11.25 StartY=45 StartZ=0 EndX=11.25 EndY=-19 EndZ=0
    g8: ArcOfCircle CenterX=9.25 CenterY=-19 CenterZ=0 NormalX=0 NormalY=0 NormalZ=1 AngleXU=0 Radius=2 StartAngle=4.71239 EndAngle=6.28319
    g9: Circle CenterX=0 CenterY=-17 CenterZ=0 NormalX=0 NormalY=0 NormalZ=1 AngleXU=0 Radius=2
    g10: Circle CenterX=-8.75 CenterY=-7.7 CenterZ=0 NormalX=0 NormalY=0 NormalZ=1 AngleXU=0 Radius=1.55
    g11: Circle CenterX=8.75 CenterY=-7.7 CenterZ=0 NormalX=0 NormalY=0 NormalZ=1 AngleXU=0 Radius=1.55
    g12: Circle CenterX=0 CenterY=42.7 CenterZ=0 NormalX=0 NormalY=0 NormalZ=1 AngleXU=0 Radius=1.5
    g13: ArcOfCircle CenterX=3.9e-14 CenterY=22.7 CenterZ=0 NormalX=0 NormalY=0 NormalZ=1 AngleXU=0 Radius=7 StartAngle=1.8505e-12 EndAngle=3.14159
    g14: ArcOfCircle CenterX=3e-16 CenterY=-0.3 CenterZ=0 NormalX=0 NormalY=0 NormalZ=1 AngleXU=0 Radius=7 StartAngle=3.14159 EndAngle=6.28319
    g15: LineSegment StartX=-7 StartY=22.7 StartZ=0 EndX=-7 EndY=-0.3 EndZ=0
    g16: LineSegment StartX=7 StartY=22.7 StartZ=0 EndX=7 EndY=-0.3 EndZ=0
    g17: LineSegment StartX=0 StartY=42.7 StartZ=0 EndX=3.9e-14 EndY=22.7 EndZ=0
  constraints (41):
    c: PointOnObject(g0,g-2)
    c: Horizontal(g1)
    c: Tangent(g1,g2) = 1.5708
    c: Vertical(g3)
    c: Tangent(g3,g4) = 1.5708
    c: Horizontal(g5)
    c: Tangent(g5,g6) = 1.5708
    c: Vertical(g7)
    c: Tangent(g7,g8) = 1.5708
    c: Tangent(g8,g1) = 1.5708
    c: Tangent(g2,g3) = 1.5708
    c: Tangent(g4,g5) = 1.5708
    c: Tangent(g6,g7) = 1.5708
    c: Coincident(g9,g-5)
    c: Coincident(g10,g-3)
    c: Coincident(g11,g-4)
    c: Diameter(g11) = 3.1
    c: Equal(g11,g10)
    c: Diameter(g9) = 4
    c: Diameter(g2) = 4
    c: Equal(g2,g8)
    c: Equal(g2,g4)
    c: Equal(g2,g6)
    c: Distance(g9,g1) = 4
    c: Distance(g4,g1) = 68
    c: Diameter(g12) = 3
    c: Tangent(g13,g16) = 1.5708
    c: Tangent(g13,g15) = -1.5708
    c: Tangent(g15,g14) = -1.5708
    c: Tangent(g16,g14) = 1.5708
    c: Vertical(g15)
    c: Symmetric(g14,g14,g-2)
    c: Diameter(g14) = 14
    c: Coincident(g17,g12)
    c: Coincident(g17,g13)
    c: Equal(g17,g0)
    c: Coincident(g12,g0)
    c: PointOnObject(g7,g-9)
    c: PointOnObject(g2,g-8)
    c: Coincident(g-10,g0)
    c: Coincident(g13,g-11)
FEATURE [PartDesign::Pad] Pad033
  Direction = (1,1,1)
  Length = 3
  Length2 = 100
  Profile = -> Sketch035
  Type = 0
FEATURE [PartDesign::Body] Body024  label="support_left"
  Group = -> [Binder012,Binder013,Sketch035,Binder014,Pad033]
  Origin = -> Origin028
  Tip = -> Pad033
FEATURE [Part::Part2DObjectPython] Shape2DView  # Draft 2D object (typed FeaturePython)
  AutoUpdate = true
  Base = -> Body
  Clip = false
  FuseArch = false
  HiddenLines = false
  InPlace = true
  OnlySolids = false
  Projection = (0,-1,0)
  ProjectionMode = 0
  SegmentLength = 0.05
  Tessellation = false
  VisibleOnly = false
FEATURE [Part::Part2DObjectPython] Shape2DView001  # Draft 2D object (typed FeaturePython)
  AutoUpdate = true
  Base = -> Body022
  Clip = false
  FuseArch = false
  HiddenLines = false
  InPlace = true
  OnlySolids = false
  Projection = (0,0,1)
  ProjectionMode = 0
  SegmentLength = 0.05
  Tessellation = false
  VisibleOnly = false
FEATURE [Part::Part2DObjectPython] Shape2DView003  # Draft 2D object (typed FeaturePython)
  AutoUpdate = true
  Base = -> Body024
  Clip = false
  FuseArch = false
  HiddenLines = false
  InPlace = true
  OnlySolids = false
  Projection = (0,-1,0)
  ProjectionMode = 0
  SegmentLength = 0.05
  Tessellation = false
  VisibleOnly = false
FEATURE [PartDesign::SubShapeBinder] Binder015
  BindCopyOnChange = 0
  BindMode = 0
  ClaimChildren = false
  Context = -> Parts [Body025.Binder015.]
  Fuse = false
  MakeFace = true
  OffsetFill = false
  OffsetIntersection = false
  OffsetJoinType = 0
  OffsetOpenResult = false
  PartialLoad = false
  Refine = true
  Relative = true
  Support = -> [Body021]
  _Version = 2
FEATURE [PartDesign::SubShapeBinder] Binder016
  BindCopyOnChange = 0
  BindMode = 0
  ClaimChildren = false
  Context = -> Parts [Body025.Binder016.]
  Fuse = false
  MakeFace = true
  OffsetFill = false
  OffsetIntersection = false
  OffsetJoinType = 0
  OffsetOpenResult = false
  PartialLoad = false
  Refine = true
  Relative = true
  Support = -> [LinkGroup]
  _Version = 2
FEATURE [Sketcher::SketchObject] Sketch036
  ExternalGeometry = -> [Binder016,Binder015]
  FullyConstrained = true
  MapMode = 5
  Placement = pos=(0,-28.3,0) rot=(1,0,0;1.5708rad)
  Support = -> [Binder016]
  sketch-geometry (2):
    g0: Circle CenterX=8.6e-15 CenterY=-28.3 CenterZ=0 NormalX=0 NormalY=0 NormalZ=1 AngleXU=0 Radius=3
    g1: Circle CenterX=8.6e-15 CenterY=-28.3 CenterZ=0 NormalX=0 NormalY=0 NormalZ=1 AngleXU=0 Radius=4.5
  constraints (4):
    c: Coincident(g0,g-3)
    c: Coincident(g1,g0)
    c: Equal(g1,g-5)
    c: Diameter(g0) = 6
FEATURE [PartDesign::Pad] Pad034
  Direction = (1,1,1)
  Length = 3
  Length2 = 100
  Profile = -> Sketch036
  Type = 0
FEATURE [PartDesign::Body] Body025  label="spacer_left"
  Group = -> [Binder015,Binder016,Sketch036,Pad034]
  Origin = -> Origin029
  Tip = -> Pad034
FEATURE [Part::Part2DObjectPython] Shape2DView004  # Draft 2D object (typed FeaturePython)
  AutoUpdate = true
  Base = -> Body025
  Clip = false
  FuseArch = false
  HiddenLines = false
  InPlace = true
  OnlySolids = false
  Projection = (0,-1,0)
  ProjectionMode = 0
  SegmentLength = 0.05
  Tessellation = false
  VisibleOnly = false
FEATURE [PartDesign::SubShapeBinder] Binder017
  BindCopyOnChange = 0
  BindMode = 0
  ClaimChildren = false
  Context = -> Parts [Body026.Binder017.]
  Fuse = false
  MakeFace = true
  OffsetFill = false
  OffsetIntersection = false
  OffsetJoinType = 0
  OffsetOpenResult = false
  PartialLoad = false
  Refine = true
  Relative = true
  Support = -> [Body]
  _Version = 2
FEATURE [PartDesign::SubShapeBinder] Binder018
  BindCopyOnChange = 0
  BindMode = 0
  ClaimChildren = false
  Context = -> Parts [Body026.Binder018.]
  Fuse = false
  MakeFace = true
  OffsetFill = false
  OffsetIntersection = false
  OffsetJoinType = 0
  OffsetOpenResult = false
  PartialLoad = false
  Refine = true
  Relative = true
  Support = -> [Body024]
  _Version = 2
FEATURE [Sketcher::SketchObject] Sketch037
  ExternalGeometry = -> [Binder018]
  FullyConstrained = true
  MapMode = 5
  Placement = pos=(9.9e-15,-49.4,-1.09e-14) rot=(1,0,0;1.5708rad)
  Support = -> [Binder017]
  sketch-geometry (27):
    g0: LineSegment StartX=-36 StartY=46.7 StartZ=0 EndX=7.1e-15 EndY=46.7 EndZ=0
    g1: LineSegment StartX=4 StartY=42.7 StartZ=0 EndX=4 EndY=6.7 EndZ=0
    g2: LineSegment StartX=4 StartY=6.7 StartZ=0 EndX=37.6906 EndY=6.7 EndZ=0
    g3: LineSegment StartX=37.6906 StartY=6.7 StartZ=0 EndX=40 EndY=10.7 EndZ=0
    g4: LineSegment StartX=40 StartY=10.7 StartZ=0 EndX=46.9282 EndY=10.7 EndZ=0
    g5: LineSegment StartX=46.9282 StartY=10.7 StartZ=0 EndX=46.9282 EndY=6.7 EndZ=0
    g6: LineSegment StartX=46.9282 StartY=6.7 StartZ=0 EndX=42.3094 EndY=6.7 EndZ=0
    g7: LineSegment StartX=42.3094 StartY=6.7 StartZ=0 EndX=40 EndY=2.7 EndZ=0
    g8: LineSegment StartX=40 StartY=2.7 StartZ=0 EndX=42.3094 EndY=-1.3 EndZ=0
    g9: LineSegment StartX=42.3094 StartY=-1.3 StartZ=0 EndX=46.9282 EndY=-1.3 EndZ=0
    g10: LineSegment StartX=46.9282 StartY=-1.3 StartZ=0 EndX=46.9282 EndY=-5.3 EndZ=0
    g11: LineSegment StartX=46.9282 StartY=-5.3 StartZ=0 EndX=40 EndY=-5.3 EndZ=0
    g12: LineSegment StartX=40 StartY=-5.3 StartZ=0 EndX=37.6906 EndY=-1.3 EndZ=0
    g13: LineSegment StartX=37.6906 StartY=-1.3 StartZ=0 EndX=7.1e-15 EndY=-1.3 EndZ=0
    g14: LineSegment StartX=-4 StartY=2.7 StartZ=0 EndX=-4 EndY=38.7 EndZ=0
    g15: LineSegment StartX=-4 StartY=38.7 StartZ=0 EndX=-36 EndY=38.7 EndZ=0
    g16: Circle CenterX=6.3e-15 CenterY=42.7 CenterZ=0 NormalX=0 NormalY=0 NormalZ=1 AngleXU=0 Radius=1.5
    g17: LineSegment StartX=6.3e-15 StartY=42.7 StartZ=0 EndX=-40 EndY=42.7 EndZ=0
    g18: LineSegment StartX=6.3e-15 StartY=42.7 StartZ=0 EndX=6.3e-15 EndY=2.7 EndZ=0
    g19: LineSegment StartX=6.3e-15 StartY=2.7 StartZ=0 EndX=40 EndY=2.7 EndZ=0
    g20: Circle CenterX=6.3e-15 CenterY=42.7 CenterZ=0 NormalX=0 NormalY=0 NormalZ=1 AngleXU=0 Radius=4
    g21: Circle CenterX=6.3e-15 CenterY=2.7 CenterZ=0 NormalX=0 NormalY=0 NormalZ=1 AngleXU=0 Radius=4
    g22: LineSegment StartX=42.3094 StartY=6.7 StartZ=0 EndX=38.8453 EndY=8.7 EndZ=0
    g23: Circle CenterX=-36 CenterY=42.7 CenterZ=0 NormalX=0 NormalY=0 NormalZ=1 AngleXU=0 Radius=0.6
    g24: ArcOfCircle CenterX=7.1e-15 CenterY=42.7 CenterZ=0 NormalX=0 NormalY=0 NormalZ=1 AngleXU=0 Radius=4 StartAngle=0 EndAngle=1.5708
    g25: ArcOfCircle CenterX=6.7e-15 CenterY=2.7 CenterZ=0 NormalX=0 NormalY=0 NormalZ=1 AngleXU=0 Radius=4 StartAngle=3.14159 EndAngle=4.71239
    g26: ArcOfCircle CenterX=-36 CenterY=42.7 CenterZ=0 NormalX=0 NormalY=0 NormalZ=1 AngleXU=0 Radius=4 StartAngle=1.5708 EndAngle=4.71239
  constraints (75):
    c: Horizontal(g0)
    c: Vertical(g1)
    c: Coincident(g1,g2)
    c: Horizontal(g2)
    c: Coincident(g2,g3)
    c: Coincident(g3,g4)
    c: Horizontal(g4)
    c: Coincident(g4,g5)
    c: Vertical(g5)
    c: Coincident(g5,g6)
    c: Horizontal(g6)
    c: Coincident(g6,g7)
    c: Coincident(g7,g8)
    c: Coincident(g8,g9)
    c: Horizontal(g9)
    c: Coincident(g9,g10)
    c: Vertical(g10)
    c: Coincident(g10,g11)
    c: Horizontal(g11)
    c: Coincident(g11,g12)
    c: Coincident(g12,g13)
    c: Horizontal(g13)
    c: Vertical(g14)
    c: Coincident(g14,g15)
    c: Horizontal(g15)
    c: Diameter(g16) = 3
    c: Coincident(g17,g16)
    c: Horizontal(g17)
    c: Coincident(g18,g16)
    c: Vertical(g18)
    c: Coincident(g19,g18)
    c: Coincident(g19,g7)
    c: Horizontal(g19)
    c: Coincident(g20,g16)
    c: Coincident(g21,g18)
    c: Diameter(g20) = 8
    c: Equal(g20,g21)
    c: Tangent(g14,g21)
    c: Tangent(g13,g21)
    c: Tangent(g0,g20)
    c: Tangent(g20,g1)
    c: Tangent(g15,g20)
    c: Tangent(g2,g21)
    c: Vertical(g2,g12)
    c: Vertical(g11,g3)
    c: Equal(g5,g10)
    c: Equal(g6,g9)
    c: Equal(g7,g8)
    c: Angle(g3) = 1.0472
    c: Angle(g8,g7) = 2.0944
    c: Vertical(g6,g8)
    c: DistanceX(g17,g17) = 40
    c: DistanceY(g18,g18) = 40
    c: DistanceX(g19,g19) = 40
    c: DistanceY(g5,g5) = 4
    c: DistanceY(g9,g5) = 8
    c: Equal(g6,g7)
    c: Coincident(g22,g6)
    c: PointOnObject(g22,g3)
    c: Perpendicular(g22,g3)
    c: Distance(g22) = 4
    c: PointOnObject(g23,g17)
    c: Diameter(g23) = 1.2
    c: Tangent(g0,g24) = 1.5708
    c: Tangent(g1,g24) = 1.5708
    c: Equal(g24,g20)
    c: Tangent(g14,g25) = 1.5708
    c: Tangent(g13,g25) = 1.5708
    c: Equal(g25,g21)
    c: Coincident(g26,g23)
    c: Vertical(g26,g23)
    c: Coincident(g0,g26)
    c: Coincident(g15,g26)
    c: DistanceX(g17,g23) = 4
    c: Coincident(g16,g-3)
FEATURE [PartDesign::Pad] Pad035
  Direction = (1,1,1)
  Length = 3
  Length2 = 100
  Profile = -> Sketch037
  Type = 0
FEATURE [PartDesign::Body] Body026  label="hand_left"
  Group = -> [Binder017,Sketch037,Binder018,Pad035]
  Origin = -> Origin030
  Tip = -> Pad035
FEATURE [PartDesign::SubShapeBinder] Binder019
  BindCopyOnChange = 0
  BindMode = 0
  ClaimChildren = false
  Context = -> Parts [Body027.Binder019.]
  Fuse = false
  MakeFace = true
  OffsetFill = false
  OffsetIntersection = false
  OffsetJoinType = 0
  OffsetOpenResult = false
  PartialLoad = false
  Refine = true
  Relative = true
  Support = -> [Body026]
  _Version = 2
FEATURE [PartDesign::SubShapeBinder] Binder020
  BindCopyOnChange = 0
  BindMode = 0
  ClaimChildren = false
  Context = -> Parts [Body027.Binder020.]
  Fuse = false
  MakeFace = true
  OffsetFill = false
  OffsetIntersection = false
  OffsetJoinType = 0
  OffsetOpenResult = false
  PartialLoad = false
  Refine = true
  Relative = true
  Support = -> [Body]
  _Version = 2
FEATURE [Sketcher::SketchObject] Sketch038
  ExternalGeometry = -> [Binder019,Binder020]
  FullyConstrained = false
  MapMode = 5
  Placement = pos=(1e-14,-52.4,-8.9e-15) rot=(1,0,0;1.5708rad)
  Support = -> [Binder019]
  sketch-geometry (8):
    g0: LineSegment StartX=-44.9735 StartY=38.2868 StartZ=0 EndX=-36 EndY=42.7 EndZ=0
    g1: LineSegment StartX=-36 StartY=42.7 StartZ=0 EndX=-6 EndY=-18.3 EndZ=0
    g2: LineSegment StartX=-6 StartY=-18.3 StartZ=0 EndX=-14.9735 EndY=-22.7132 EndZ=0
    g3: LineSegment StartX=-44.9735 StartY=38.2868 StartZ=0 EndX=-44.5322 EndY=37.3895 EndZ=0
    g4: LineSegment StartX=-44.5322 StartY=37.3895 StartZ=0 EndX=-36.456 EndY=41.3613 EndZ=0
    g5: LineSegment StartX=-36.456 StartY=41.3613 StartZ=0 EndX=-7.33867 EndY=-17.844 EndZ=0
    g6: LineSegment StartX=-7.33867 StartY=-17.844 StartZ=0 EndX=-15.4148 EndY=-21.8158 EndZ=0
    g7: LineSegment StartX=-15.4148 StartY=-21.8158 StartZ=0 EndX=-14.9735 EndY=-22.7132 EndZ=0
  constraints (21):
    c: Coincident(g0,g-3)
    c: Coincident(g0,g1)
    c: Coincident(g1,g2)
    c: Perpendicular(g1,g0)
    c: Perpendicular(g2,g1)
    c: Equal(g0,g2)
    c: Distance(g0) = 10
    c: Coincident(g3,g0)
    c: Coincident(g3,g4)
    c: Coincident(g4,g5)
    c: Coincident(g5,g6)
    c: Coincident(g6,g7)
    c: Coincident(g7,g2)
    c: Parallel(g7,g1)
    c: Parallel(g6,g2)
    c: Parallel(g3,g1)
    c: Parallel(g4,g0)
    c: Equal(g3,g7)
    c: Equal(g6,g4)
    c: Distance(g3) = 1
    c: Distance(g4,g1) = 1
FEATURE [PartDesign::Pad] Pad036
  Direction = (1,1,1)
  Length = 1
  Length2 = 100
  Profile = -> Sketch038
  Type = 0
FEATURE [PartDesign::Body] Body027  label="wire"
  Group = -> [Binder019,Binder020,Sketch038,Pad036]
  Origin = -> Origin031
  Tip = -> Pad036
FEATURE [Part::Part2DObjectPython] Shape2DView005  # Draft 2D object (typed FeaturePython)
  AutoUpdate = true
  Base = -> Body026
  Clip = false
  FuseArch = false
  HiddenLines = false
  InPlace = true
  OnlySolids = false
  Projection = (0,-1,0)
  ProjectionMode = 0
  SegmentLength = 0.05
  Tessellation = false
  VisibleOnly = false
FEATURE [Part::Part2DObjectPython] Shape2DView006  # Draft 2D object (typed FeaturePython)
  AutoUpdate = true
  Base = -> Body027
  Clip = false
  FuseArch = false
  HiddenLines = false
  InPlace = true
  OnlySolids = false
  Projection = (0,-1,0)
  ProjectionMode = 0
  SegmentLength = 0.05
  Tessellation = false
  VisibleOnly = false
FEATURE [PartDesign::SubShapeBinder] Binder021
  BindCopyOnChange = 0
  BindMode = 0
  ClaimChildren = false
  Context = -> Parts [Body028.Binder021.]
  Fuse = false
  MakeFace = true
  OffsetFill = false
  OffsetIntersection = false
  OffsetJoinType = 0
  OffsetOpenResult = false
  PartialLoad = false
  Refine = true
  Relative = true
  Support = -> [LinkGroup]
  _Version = 2
FEATURE [Sketcher::SketchObject] Sketch039
  ExternalGeometry = -> [Binder021]
  FullyConstrained = true
  MapMode = 5
  Placement = pos=(11.25,0,-2.7e-15) rot=(0.57735,0.57735,0.57735;2.0944rad)
  Support = -> [Binder021]
  sketch-geometry (20):
    g0: LineSegment StartX=-28.3 StartY=-2.65 StartZ=0 EndX=-28.3 EndY=-40.65 EndZ=0
    g1: ArcOfCircle CenterX=-26.3 CenterY=-40.65 CenterZ=0 NormalX=0 NormalY=0 NormalZ=1 AngleXU=0 Radius=2 StartAngle=3.14159 EndAngle=4.71239
    g2: LineSegment StartX=-26.3 StartY=-42.65 StartZ=0 EndX=-11.5 EndY=-42.65 EndZ=0
    g3: ArcOfCircle CenterX=-11.5 CenterY=-40.65 CenterZ=0 NormalX=0 NormalY=0 NormalZ=1 AngleXU=0 Radius=2 StartAngle=4.71239 EndAngle=6.28319
    g4: LineSegment StartX=-9.5 StartY=-40.65 StartZ=0 EndX=-9.5 EndY=-2.65 EndZ=0
    g5: LineSegment StartX=-9.5 StartY=-2.65 StartZ=0 EndX=-9.5 EndY=25.35 EndZ=0
    g6: LineSegment StartX=-9.5 StartY=25.35 StartZ=0 EndX=-14.5 EndY=25.35 EndZ=0
    g7: LineSegment StartX=-14.5 StartY=25.35 StartZ=0 EndX=-14.5 EndY=30.35 EndZ=0
    g8: LineSegment StartX=-14.5 StartY=30.35 StartZ=0 EndX=-12.5 EndY=30.35 EndZ=0
    g9: ArcOfCircle CenterX=-12.5 CenterY=33.35 CenterZ=0 NormalX=0 NormalY=0 NormalZ=1 AngleXU=0 Radius=3 StartAngle=4.71239 EndAngle=6.28319
    g10: LineSegment StartX=-9.5 StartY=33.35 StartZ=0 EndX=-9.5 EndY=43.35 EndZ=0
    g11: ArcOfCircle CenterX=-12.5 CenterY=43.35 CenterZ=0 NormalX=0 NormalY=0 NormalZ=1 AngleXU=0 Radius=3 StartAngle=5e-16 EndAngle=1.5708
    g12: LineSegment StartX=-12.5 StartY=46.35 StartZ=0 EndX=-25.3 EndY=46.35 EndZ=0
    g13: ArcOfCircle CenterX=-25.3 CenterY=43.35 CenterZ=0 NormalX=0 NormalY=0 NormalZ=1 AngleXU=0 Radius=3 StartAngle=1.5708 EndAngle=3.14159
    g14: LineSegment StartX=-28.3 StartY=43.35 StartZ=0 EndX=-28.3 EndY=33.35 EndZ=0
    g15: ArcOfCircle CenterX=-25.3 CenterY=33.35 CenterZ=0 NormalX=0 NormalY=0 NormalZ=1 AngleXU=0 Radius=3 StartAngle=3.14159 EndAngle=4.71239
    g16: LineSegment StartX=-25.3 StartY=30.35 StartZ=0 EndX=-23.3 EndY=30.35 EndZ=0
    g17: LineSegment StartX=-23.3 StartY=30.35 StartZ=0 EndX=-23.3 EndY=25.35 EndZ=0
    g18: LineSegment StartX=-23.3 StartY=25.35 StartZ=0 EndX=-28.3 EndY=25.35 EndZ=0
    g19: LineSegment StartX=-28.3 StartY=25.35 StartZ=0 EndX=-28.3 EndY=-2.65 EndZ=0
  constraints (52):
    c: Coincident(g-3,g0)
    c: Vertical(g0)
    c: Tangent(g0,g1) = -1.5708
    c: Horizontal(g2)
    c: Tangent(g2,g3) = -1.5708
    c: Coincident(g4,g-4)
    c: Vertical(g4)
    c: Coincident(g4,g5)
    c: Vertical(g5)
    c: Coincident(g5,g6)
    c: Horizontal(g6)
    c: Coincident(g6,g7)
    c: Vertical(g7)
    c: Coincident(g7,g8)
    c: Horizontal(g8)
    c: Tangent(g8,g9) = -1.5708
    c: Vertical(g10)
    c: Tangent(g10,g11) = -1.5708
    c: Horizontal(g12)
    c: Tangent(g12,g13) = -1.5708
    c: Vertical(g14)
    c: Tangent(g14,g15) = -1.5708
    c: Horizontal(g16)
    c: Coincident(g16,g17)
    c: Vertical(g17)
    c: Coincident(g17,g18)
    c: Horizontal(g18)
    c: Coincident(g18,g19)
    c: Coincident(g19,g0)
    c: Vertical(g19)
    c: Diameter(g1) = 4
    c: Equal(g1,g3)
    c: Tangent(g3,g4) = -1.5708
    c: Tangent(g1,g2) = -1.5708
    c: Distance(g0,g2) = 40
    c: Equal(g19,g5)
    c: Equal(g18,g6)
    c: Equal(g17,g7)
    c: Equal(g16,g8)
    c: Tangent(g9,g10) = -1.5708
    c: Tangent(g11,g12) = -1.5708
    c: Tangent(g13,g14) = -1.5708
    c: Tangent(g15,g16) = -1.5708
    c: Equal(g10,g14)
    c: Diameter(g15) = 6
    c: Equal(g13,g15)
    c: Equal(g9,g15)
    c: Vertical(g14,g18)
    c: DistanceX(g18,g18) = 5
    c: DistanceY(g17,g17) = 5
    c: Distance(g16,g12) = 16
    c: DistanceY(g19,g19) = 28
FEATURE [PartDesign::Pad] Pad037
  Direction = (1,1,1)
  Length = 3
  Length2 = 100
  Profile = -> Sketch039
  Type = 0
FEATURE [PartDesign::Body] Body028  label="face"
  Group = -> [Binder021,Sketch039,Pad037]
  Origin = -> Origin032
  Tip = -> Pad037
FEATURE [Part::Part2DObjectPython] Shape2DView007  # Draft 2D object (typed FeaturePython)
  AutoUpdate = true
  Base = -> Body028
  Clip = false
  FuseArch = false
  HiddenLines = false
  InPlace = true
  OnlySolids = false
  Projection = (1,0,0)
  ProjectionMode = 0
  SegmentLength = 0.05
  Tessellation = false
  VisibleOnly = false
FEATURE [App::DocumentObjectGroup] Group  label="DXF"
  Group = -> [Shape2DView,Shape2DView001,Shape2DView003,Shape2DView004,Shape2DView005,Shape2DView006,Shape2DView007]
FEATURE [PartDesign::FeatureBase] Clone
  BaseFeature = -> Body021
  Placement = pos=(-27,-18.9,-28.3) rot=(0.57735,0.57735,-0.57735;2.0944rad)
FEATURE [PartDesign::Body] Body029  label="cam_3Dp_motor_right"
  BaseFeature = -> Body021
  Group = -> [Clone]
  Origin = -> Origin033
  Placement = pos=(-1.7e-14,-37.9,-56.6) rot=(1,0,0;3.14159rad)
  Tip = -> Clone
FEATURE [PartDesign::FeatureBase] Clone001
  BaseFeature = -> Body025
FEATURE [PartDesign::Body] Body030  label="spacer_right"
  Group = -> [Clone001]
  Origin = -> Origin034
  Placement = pos=(4e-15,-37.8,-1.8e-14) rot=(0,0,1;3.14159rad)
  Tip = -> Clone001
FEATURE [PartDesign::FeatureBase] Clone002
  BaseFeature = -> Body024
FEATURE [PartDesign::Body] Body031  label="support_right"
  Group = -> [Clone002]
  Origin = -> Origin035
  Placement = pos=(-2e-15,-37.8,4e-15) rot=(0,0,1;3.14159rad)
  Tip = -> Clone002
FEATURE [PartDesign::FeatureBase] Clone003
  BaseFeature = -> Body
FEATURE [PartDesign::Body] Body032  label="leg_right"
  Group = -> [Clone003]
  Origin = -> Origin036
  Placement = pos=(1e-14,-37.9,20) rot=(0,0,1;3.14159rad)
  Tip = -> Clone003
FEATURE [PartDesign::FeatureBase] Clone004
  BaseFeature = -> Body022
FEATURE [PartDesign::Body] Body033  label="feet_right"
  Group = -> [Clone004]
  Origin = -> Origin037
  Placement = pos=(0,-37.9,-139.6) rot=(1,0,0;3.14159rad)
  Tip = -> Clone004
FEATURE [PartDesign::SubShapeBinder] Binder022  label="Binder022(LinkGroup)"
  BindCopyOnChange = 0
  BindMode = 0
  ClaimChildren = false
  Context = -> Parts [Body034.Binder022.]
  Fuse = false
  MakeFace = true
  OffsetFill = false
  OffsetIntersection = false
  OffsetJoinType = 0
  OffsetOpenResult = false
  PartialLoad = false
  Relative = true
  Support = -> [LinkGroup]
  _Version = 8
FEATURE [PartDesign::Plane] DatumPlane
  AttachmentOffset = pos=(0,0,0) rot=(1,0,0;1.5708rad)
  Length = 60
  MapMode = 8
  Placement = pos=(5,-19.55,24.7) rot=(1,0,0;1.5708rad)
  ResizeMode = 0
  Support = -> [Binder022]
  Width = 60
FEATURE [PartDesign::Plane] DatumPlane001
  AttachmentOffset = pos=(0,0,-9.4) rot=(0,0,1;0rad)
  Length = 60
  MapMode = 5
  Placement = pos=(0,-18.9,-2.1e-15) rot=(1,0,0;1.5708rad)
  ResizeMode = 0
  Support = -> [Binder022]
  Width = 60
FEATURE [Sketcher::SketchObject] Sketch040
  ExternalGeometry = -> [Binder022]
  FullyConstrained = true
  MapMode = 5
  Placement = pos=(0,-18.9,-4e-15) rot=(1,0,0;1.5708rad)
  Support = -> [DatumPlane001]
  sketch-geometry (1):
    g0: Circle CenterX=8.75 CenterY=-7.7 CenterZ=0 NormalX=0 NormalY=0 NormalZ=1 AngleXU=0 Radius=1.5
  constraints (2):
    c: Coincident(g0,g-3)
    c: Diameter(g0) = 3
FEATURE [PartDesign::Pad] Pad038
  Direction = (1,1,1)
  Length = 28
  Length2 = 100
  Midplane = true
  Placement = pos=(0,-18.9,-4e-15) rot=(1,0,0;1.5708rad)
  Profile = -> Sketch040
  Type = 0
FEATURE [PartDesign::Body] Body034  label="skewer_001"
  Group = -> [Binder022,DatumPlane,Sketch040,Pad038,DatumPlane001]
  Origin = -> Origin038
  Tip = -> Pad038
FEATURE [PartDesign::FeatureBase] Clone005
  BaseFeature = -> Body034
FEATURE [PartDesign::Body] Body035  label="skewer_002"
  Group = -> [Clone005]
  Origin = -> Origin039
  Placement = pos=(-17.5,0,0) rot=(0,0,1;0rad)
  Tip = -> Clone005
FEATURE [PartDesign::Plane] DatumPlane002
  AttachmentOffset = pos=(0,0,-9.4) rot=(0,0,1;0rad)
  Length = 60
  MapMode = 5
  Placement = pos=(0,-18.9,-4e-15) rot=(1,0,0;1.5708rad)
  ResizeMode = 0
  Width = 60
FEATURE [Sketcher::SketchObject] Sketch041
  FullyConstrained = true
  MapMode = 5
  Placement = pos=(0,-18.9,-4e-15) rot=(1,0,0;1.5708rad)
  Support = -> [DatumPlane002]
  sketch-geometry (1):
    g0: Circle CenterX=0 CenterY=42.7 CenterZ=0 NormalX=0 NormalY=0 NormalZ=1 AngleXU=0 Radius=1.5
  constraints (2):
    c: Coincident(g0,g-3)
    c: Diameter(g0) = 3
FEATURE [PartDesign::Pad] Pad039
  Direction = (1,1,1)
  Length = 80
  Length2 = 100
  Midplane = true
  Placement = pos=(0,-18.9,-4e-15) rot=(1,0,0;1.5708rad)
  Profile = -> Sketch041
  Type = 0
FEATURE [PartDesign::Body] Body036  label="skewer_003"
  Group = -> [DatumPlane002,Sketch041,Pad039]
  Origin = -> Origin040
  Tip = -> Pad039
FEATURE [PartDesign::Plane] DatumPlane003
  AttachmentOffset = pos=(0,0,-9.4) rot=(0,0,1;0rad)
  Length = 60
  MapMode = 5
  Placement = pos=(0,-18.9,-4e-15) rot=(1,0,0;1.5708rad)
  ResizeMode = 0
  Width = 60
FEATURE [Sketcher::SketchObject] Sketch042
  FullyConstrained = true
  MapMode = 5
  Placement = pos=(0,-18.9,-4e-15) rot=(1,0,0;1.5708rad)
  Support = -> [DatumPlane003]
  sketch-geometry (2):
    g0: Circle CenterX=0 CenterY=42.7 CenterZ=0 NormalX=0 NormalY=0 NormalZ=1 AngleXU=0 Radius=1.6
    g1: Circle CenterX=0 CenterY=42.7 CenterZ=0 NormalX=0 NormalY=0 NormalZ=1 AngleXU=0 Radius=2.6
  constraints (4):
    c: Coincident(g0,g-3)
    c: Coincident(g1,g0)
    c: Diameter(g0) = 3.2
    c: Diameter(g1) = 5.2
FEATURE [PartDesign::Pad] Pad040
  Direction = (1,1,1)
  Length = 18
  Length2 = 100
  Midplane = true
  Placement = pos=(0,-18.9,-4e-15) rot=(1,0,0;1.5708rad)
  Profile = -> Sketch042
  Type = 0
FEATURE [PartDesign::Body] Body037  label="tube_001"
  Group = -> [DatumPlane003,Sketch042,Pad040]
  Origin = -> Origin041
  Tip = -> Pad040
FEATURE [PartDesign::Plane] DatumPlane004
  AttachmentOffset = pos=(0,0,0.4) rot=(0,0,1;0rad)
  Length = 60
  MapMode = 5
  Placement = pos=(0,-31.7,-7e-15) rot=(1,0,0;1.5708rad)
  ResizeMode = 0
  Width = 60
FEATURE [Sketcher::SketchObject] Sketch043
  FullyConstrained = true
  MapMode = 5
  Placement = pos=(0,-31.7,-7e-15) rot=(1,0,0;1.5708rad)
  Support = -> [DatumPlane004]
  sketch-geometry (2):
    g0: Circle CenterX=0 CenterY=42.7 CenterZ=0 NormalX=0 NormalY=0 NormalZ=1 AngleXU=0 Radius=1.6
    g1: Circle CenterX=0 CenterY=42.7 CenterZ=0 NormalX=0 NormalY=0 NormalZ=1 AngleXU=0 Radius=2.6
  constraints (4):
    c: Coincident(g0,g-4)
    c: Coincident(g1,g0)
    c: Equal(g0,g-3)
    c: Equal(g-4,g1)
FEATURE [PartDesign::Pad] Pad041
  Direction = (1,1,1)
  Length = 14.5
  Length2 = 100
  Placement = pos=(0,-31.7,-7e-15) rot=(1,0,0;1.5708rad)
  Profile = -> Sketch043
  Type = 0
FEATURE [PartDesign::Body] Body038  label="tube_002"
  Group = -> [DatumPlane004,Sketch043,Pad041]
  Origin = -> Origin042
  Tip = -> Pad041
FEATURE [PartDesign::FeatureBase] Clone006
  BaseFeature = -> Body038
FEATURE [PartDesign::Body] Body039  label="tube_003"
  Group = -> [Clone006]
  Origin = -> Origin043
  Placement = pos=(-5e-15,-38,0) rot=(0,0,1;3.14159rad)
  Tip = -> Clone006
FEATURE [PartDesign::FeatureBase] Clone007
  BaseFeature = -> Body026
FEATURE [PartDesign::Body] Body040  label="hand_right"
  Group = -> [Clone007]
  Origin = -> Origin044
  Placement = pos=(0,63.9,0) rot=(0,0,1;0rad)
  Tip = -> Clone007
FEATURE [PartDesign::Plane] DatumPlane005
  AttachmentOffset = pos=(0,0,0.5) rot=(0,0,1;0rad)
  Length = 60
  MapMode = 5
  Placement = pos=(1e-14,-52.9,-9e-15) rot=(1,0,0;1.5708rad)
  ResizeMode = 0
  Width = 60
FEATURE [Sketcher::SketchObject] Sketch044
  FullyConstrained = true
  MapMode = 5
  Placement = pos=(1e-14,-52.9,-9e-15) rot=(1,0,0;1.5708rad)
  Support = -> [DatumPlane005]
  sketch-geometry (2):
    g0: Circle CenterX=-1.12e-14 CenterY=42.7 CenterZ=0 NormalX=0 NormalY=0 NormalZ=1 AngleXU=0 Radius=1.4
    g1: Circle CenterX=-1.12e-14 CenterY=42.7 CenterZ=0 NormalX=0 NormalY=0 NormalZ=1 AngleXU=0 Radius=5
  constraints (4):
    c: Coincident(g0,g-3)
    c: Coincident(g1,g0)
    c: Diameter(g0) = 2.8
    c: Diameter(g1) = 10
FEATURE [PartDesign::Pad] Pad042
  Direction = (1,1,1)
  Length = 3
  Length2 = 100
  Placement = pos=(1e-14,-52.9,-9e-15) rot=(1,0,0;1.5708rad)
  Profile = -> Sketch044
  Type = 0
FEATURE [PartDesign::Body] Body041  label="glue_stick_lock_001"
  Group = -> [DatumPlane005,Sketch044,Pad042]
  Origin = -> Origin045
  Tip = -> Pad042
FEATURE [PartDesign::FeatureBase] Clone008
  BaseFeature = -> Body041
FEATURE [PartDesign::Body] Body042  label="glue_stick_lock_002"
  Group = -> [Clone008]
  Origin = -> Origin046
  Placement = pos=(-5e-15,-37.9,0) rot=(0,0,1;3.14159rad)
  Tip = -> Clone008
FEATURE [App::DocumentObjectGroup] Parts
  Group = -> [Body021,Body,Body001,Compound,Body022,Body024,Body025,Body026,Body027,Body028,Body029,Body030,Body031,Body032,Body033,Body034,Body035,Body036,Body037,Body038,Body039,Body040,Body041,Body042]
